# Revit family: AtticStairs_Fakro_LWP
name_source: partatom
category: Generic Models
units: mm (PartAtom-declared; Revit-internal decimal feet)

## family parameters
Always vertical = Yes
Can host rebar = No
Classification Number = 23.30.70.21.17
Cut with Voids When Loaded = No
Host = Floor
Maintain Annotation Orientation = No
Part Type = Normal
Room Calculation Point = No
Round Connector Dimension = Use Diameter
Shared = No

## types (5) — shared parameters
Assembly Code = C1020700
Keynote = 11 30 33
Manufacturer = Fakro USA
Manufacturer Fax = 630-543-1011
Manufacturer Website = http://www.fakrousa.com
Maximum Safe Load = 250.00 lb
Model = LWP
Revision = R1_2016-01
Sales Information = http://www.fakrousa.com
URL = http://www.fakrousa.com
zero-valued in all types: Cost, Default Elevation, Expected Lifespan (Years), Maintenance Schedule (Months), Warranty Duration (Years)

## per-type parameters (varying)
| type | Description | Door Height | Door Width | Mechanism width | Overall Length | Overall Width |
| 30x54 | Fakro LWP Attic Stairs - 30x54 | 1321 mm | 711 mm | 673 mm | 1359 mm | 749 mm |
| 25x54 | Fakro LWP Attic Stairs - 25x54 | 1321 mm | 584 mm | 546 mm | 1359 mm | 622 mm |
| 22x54 | Fakro LWP Attic Stairs - 22x54 | 1321 mm | 521 mm | 483 mm | 1359 mm | 559 mm |
| 25x47 | Fakro LWP Attic Stairs - 25x47 | 1146 mm | 584 mm | 546 mm | 1184 mm | 622 mm |
| 22x47 | Fakro LWP Attic Stairs - 22x47 | 1146 mm | 521 mm | 483 mm | 1184 mm | 559 mm |

## geometry (parser evidence)
native form markers: Blend x2
no freeform markers — native parametric forms only
